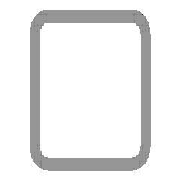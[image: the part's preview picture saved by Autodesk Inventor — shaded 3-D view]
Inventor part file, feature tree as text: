
AUTODESK INVENTOR PART (.ipt)
format: ipt  version: 2021 (Build 250183000, 183)  size: 141,312 bytes
history: native  units: mm (DEFAULTED — no unit token found)
features: other x5, sketch x3, extrude x1, split x1, plane x1
ambient origin geometry x8: Origin, YZ Plane, XZ Plane, XY Plane, X Axis, Y Axis, Z Axis, Center Point
bodies: Solid1 (feature_tree)
feature tree (11):
  parser-record x1  (decoder bookkeeping rows leaked as tree rows — omitted from the tree; the rows remain in map.json)
  other  "Driven Length"
  other  "Plano inicial"
  other  "Plano final"
  extrude  "Corpo"  TaperAngle=0.0deg  [1 undecoded]
  other  "Plano de trabalho4"
  split  "Dividir1"
  sketch  "Esboço"  dims[d11=50.8mm d12=4.7625mm d13=-0.0mm d14=1015.698063mm d15=25.4mm d16=25.4mm d17=9.525mm d18=90.0deg d19=1015.698063mm]
  sketch  "Sketch3"  dims[d3=1015.698063mm d4=0.0mm]
  plane  "Work Plane3"
  sketch  "Sketch4"  dims[d10=50.8mm]
note: 1 required parameter value undecoded (feature->parameter linkage not recoverable at this tier; creation-order binding heuristic only, values carry confidence <= 0.55)
